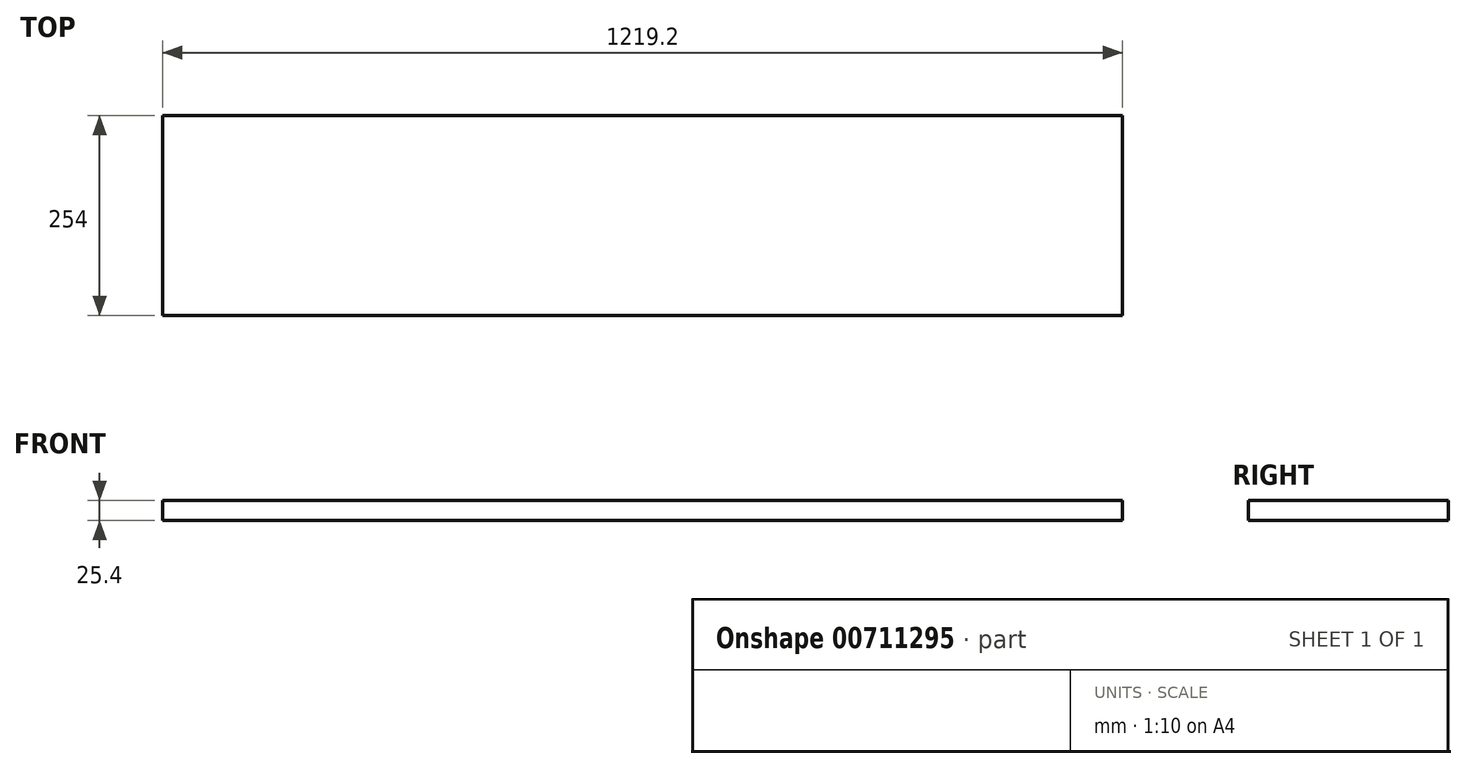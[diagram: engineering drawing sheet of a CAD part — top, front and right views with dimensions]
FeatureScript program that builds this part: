
annotation { "Feature Type Name" : "Feature", "Feature Type Description" : "" }
export const myFeature = defineFeature(function(context is Context, id is Id, definition is map)
    precondition{}
    {
        {
            var Q0;
            Q0=qCreatedBy(makeId("Top.planeOp"),FACE);
            var sketch = newSketch(context, id + "F0", { "sketchPlane" : qUnion([Q0])});
            skLineSegment(sketch, "E0.bottom", {"start": v(-281, 128.32) * mm, "end": v(938.2, 128.32) * mm});
            skLineSegment(sketch, "E0.top", {"start": v(-281, -125.68) * mm, "end": v(938.2, -125.68) * mm});
            skLineSegment(sketch, "E0.left", {"start": v(-281, 128.32) * mm, "end": v(-281, -125.68) * mm});
            skLineSegment(sketch, "E0.right", {"start": v(938.2, 128.32) * mm, "end": v(938.2, -125.68) * mm});
            skSolve(sketch);
        }
        {
            var Q0;
            Q0=makeQuery(id+"F0.imprint","IMPRINT",FACE,{"disambiguationData":[TD([[makeQuery(id+"F0.imprint","IMPRINT",EDGE,{"derivedFrom":sQuery(id+"F0.wireOp",EDGE,"E0.bottom")}),-1.0]])]});
            extrude(context, id + "F1", {"entities" : qUnion([Q0]), "endBound" : BoundingType.SYMMETRIC, "depth" : 25.4 * mm, "offsetDistance" : 25.4 * mm});
        }
    });
